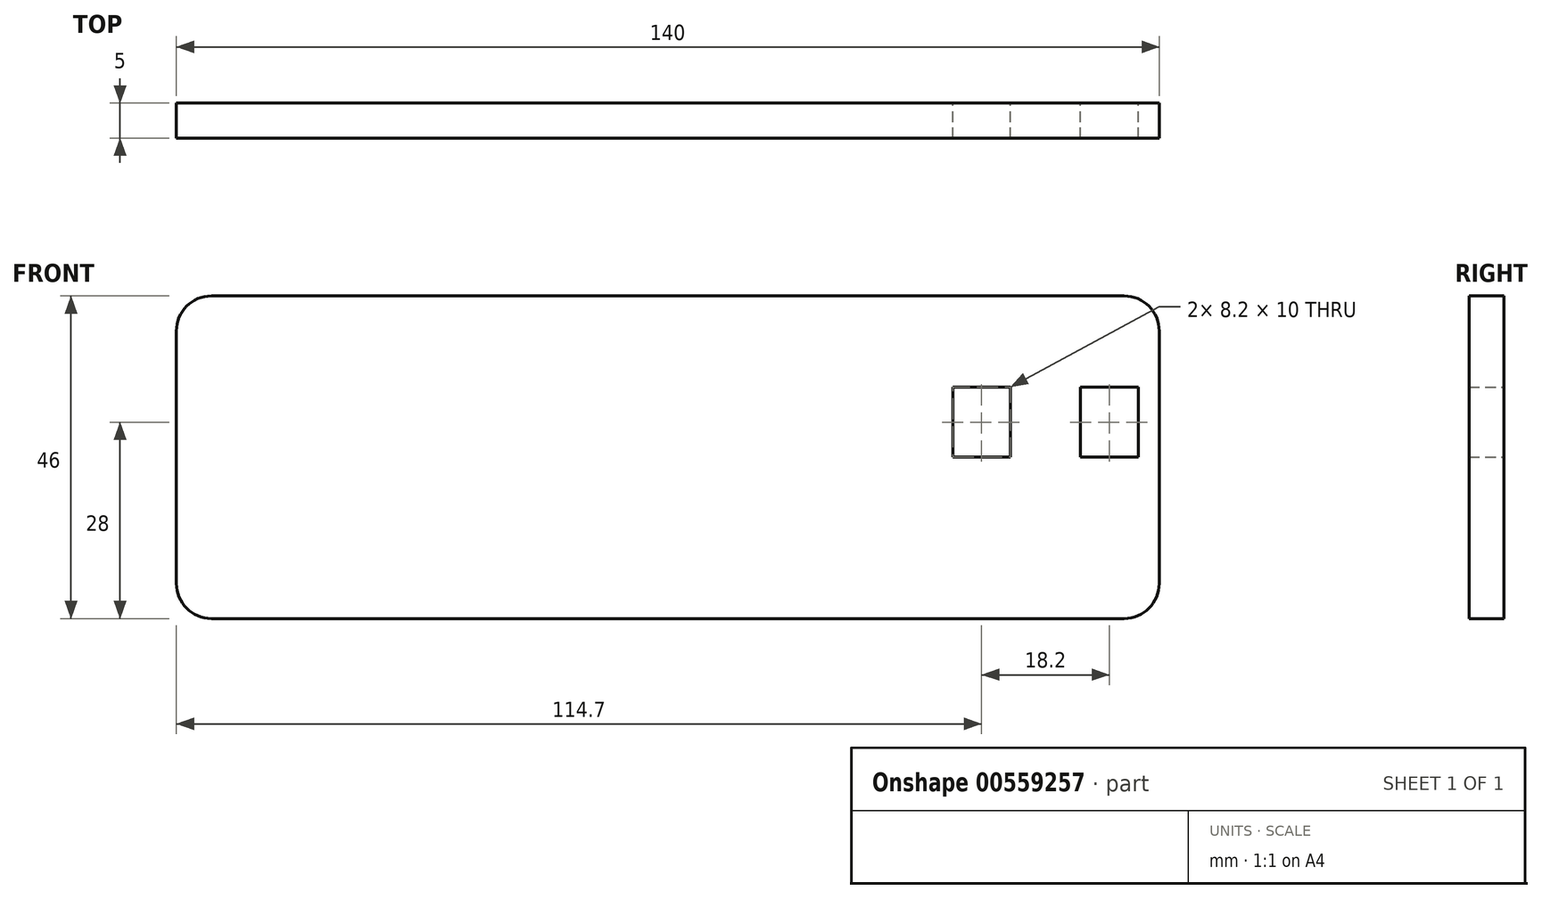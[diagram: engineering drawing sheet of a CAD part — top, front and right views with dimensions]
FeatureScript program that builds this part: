
annotation { "Feature Type Name" : "Feature", "Feature Type Description" : "" }
export const myFeature = defineFeature(function(context is Context, id is Id, definition is map)
    precondition{}
    {
        {
            var Q0;
            Q0=qCreatedBy(makeId("Front.planeOp"),FACE);
            var sketch = newSketch(context, id + "F0", { "sketchPlane" : qUnion([Q0])});
            skLineSegment(sketch, "E0.bottom", {"start": v(70, 23) * mm, "end": v(-70, 23) * mm});
            skLineSegment(sketch, "E0.top", {"start": v(70, -23) * mm, "end": v(-70, -23) * mm});
            skLineSegment(sketch, "E0.left", {"start": v(70, 23) * mm, "end": v(70, -23) * mm});
            skLineSegment(sketch, "E0.right", {"start": v(-70, 23) * mm, "end": v(-70, -23) * mm});
            skPoint(sketch, "E0.middle", {"position": v(0, 0) * mm});
            skLineSegment(sketch, "E1.bottom", {"start": v(70, 23) * mm, "end": v(25, 23) * mm});
            skLineSegment(sketch, "E1.top", {"start": v(70, -23) * mm, "end": v(25, -23) * mm});
            skLineSegment(sketch, "E1.right", {"start": v(25, 23) * mm, "end": v(25, -23) * mm});
            skPoint(sketch, "E1.middle", {"position": v(47.5, 0) * mm});
            skLineSegment(sketch, "E2.bottom", {"start": v(40.6, 10) * mm, "end": v(48.8, 10) * mm});
            skLineSegment(sketch, "E2.top", {"start": v(40.6, 0) * mm, "end": v(48.8, 0) * mm});
            skLineSegment(sketch, "E2.left", {"start": v(40.6, 10) * mm, "end": v(40.6, 0) * mm});
            skLineSegment(sketch, "E2.right", {"start": v(48.8, 10) * mm, "end": v(48.8, 0) * mm});
            skLineSegment(sketch, "E3.bottom", {"start": v(58.8, 10) * mm, "end": v(67, 10) * mm});
            skLineSegment(sketch, "E3.top", {"start": v(58.8, 0) * mm, "end": v(67, 0) * mm});
            skLineSegment(sketch, "E3.left", {"start": v(58.8, 10) * mm, "end": v(58.8, 0) * mm});
            skLineSegment(sketch, "E3.right", {"start": v(67, 10) * mm, "end": v(67, 0) * mm});
            skSolve(sketch);
        }
        {
            var Q0;
            Q0=qSketchRegion(id+"F0",true);
            extrude(context, id + "F1", {"entities" : qUnion([Q0]), "endBound" : BoundingType.SYMMETRIC, "depth" : 10 * mm, "offsetDistance" : 25 * mm});
        }
        {
            var Q0;
            Q0=qSketchRegion(id+"F0",true);
            extrude(context, id + "F2", {"entities" : qUnion([Q0]), "operationType" : NewBodyOperationType.REMOVE, "oppositeDirection" : true, "depth" : 25 * mm, "offsetDistance" : 25 * mm});
        }
        {
            var Q0;
            Q0=makeQuery(id+"F1.opExtrude","SWEPT_EDGE",EDGE,{"disambiguationData":[OSD([sQuery(id+"F0.wireOp",EDGE,"E0.bottom"),sQuery(id+"F0.wireOp",EDGE,"E0.right")])]});
            var Q1;
            Q1=makeQuery(id+"F1.opExtrude","SWEPT_EDGE",EDGE,{"disambiguationData":[OSD([sQuery(id+"F0.wireOp",EDGE,"E0.top"),sQuery(id+"F0.wireOp",EDGE,"E0.right")])]});
            var Q2;
            Q2=makeQuery(id+"F1.opExtrude","SWEPT_EDGE",EDGE,{"disambiguationData":[OSD([sQuery(id+"F0.wireOp",EDGE,"E1.bottom"),sQuery(id+"F0.wireOp",EDGE,"E0.left")])]});
            var Q3;
            Q3=makeQuery(id+"F1.opExtrude","SWEPT_EDGE",EDGE,{"disambiguationData":[OSD([sQuery(id+"F0.wireOp",EDGE,"E1.top"),sQuery(id+"F0.wireOp",EDGE,"E0.left")])]});
            fillet(context, id + "F3", {"entities" : qUnion([Q0, Q1, Q2, Q3]), "radius" : 5 * mm, "tangentPropagation" : true, "allowEdgeOverflow" : false});
        }
    });
